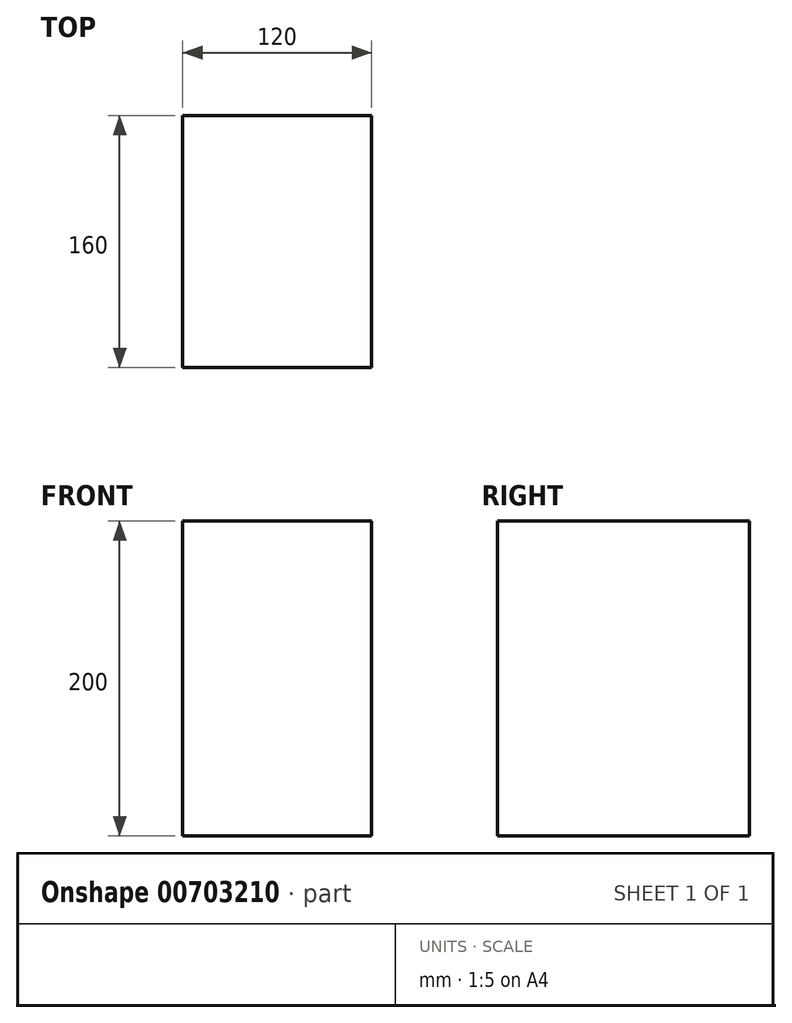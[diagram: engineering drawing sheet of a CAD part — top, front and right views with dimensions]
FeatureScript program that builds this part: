
annotation { "Feature Type Name" : "Feature", "Feature Type Description" : "" }
export const myFeature = defineFeature(function(context is Context, id is Id, definition is map)
    precondition{}
    {
        {
            var Q0;
            Q0=qCreatedBy(makeId("Front.planeOp"),FACE);
            var sketch = newSketch(context, id + "F0", { "sketchPlane" : qUnion([Q0])});
            skLineSegment(sketch, "E0.bottom", {"start": v(-67.19, 140.38) * mm, "end": v(52.81, 140.38) * mm});
            skLineSegment(sketch, "E0.top", {"start": v(-67.19, -59.62) * mm, "end": v(52.81, -59.62) * mm});
            skLineSegment(sketch, "E0.left", {"start": v(-67.19, 140.38) * mm, "end": v(-67.19, -59.62) * mm});
            skLineSegment(sketch, "E0.right", {"start": v(52.81, 140.38) * mm, "end": v(52.81, -59.62) * mm});
            skSolve(sketch);
        }
        {
            var Q0;
            Q0=makeQuery(id+"F0.imprint","IMPRINT",FACE,{"disambiguationData":[TD([[makeQuery(id+"F0.imprint","IMPRINT",EDGE,{"derivedFrom":sQuery(id+"F0.wireOp",EDGE,"E0.bottom")}),-1.0]])]});
            extrude(context, id + "F1", {"entities" : qUnion([Q0]), "depth" : 160 * mm, "offsetDistance" : 25 * mm});
        }
    });
